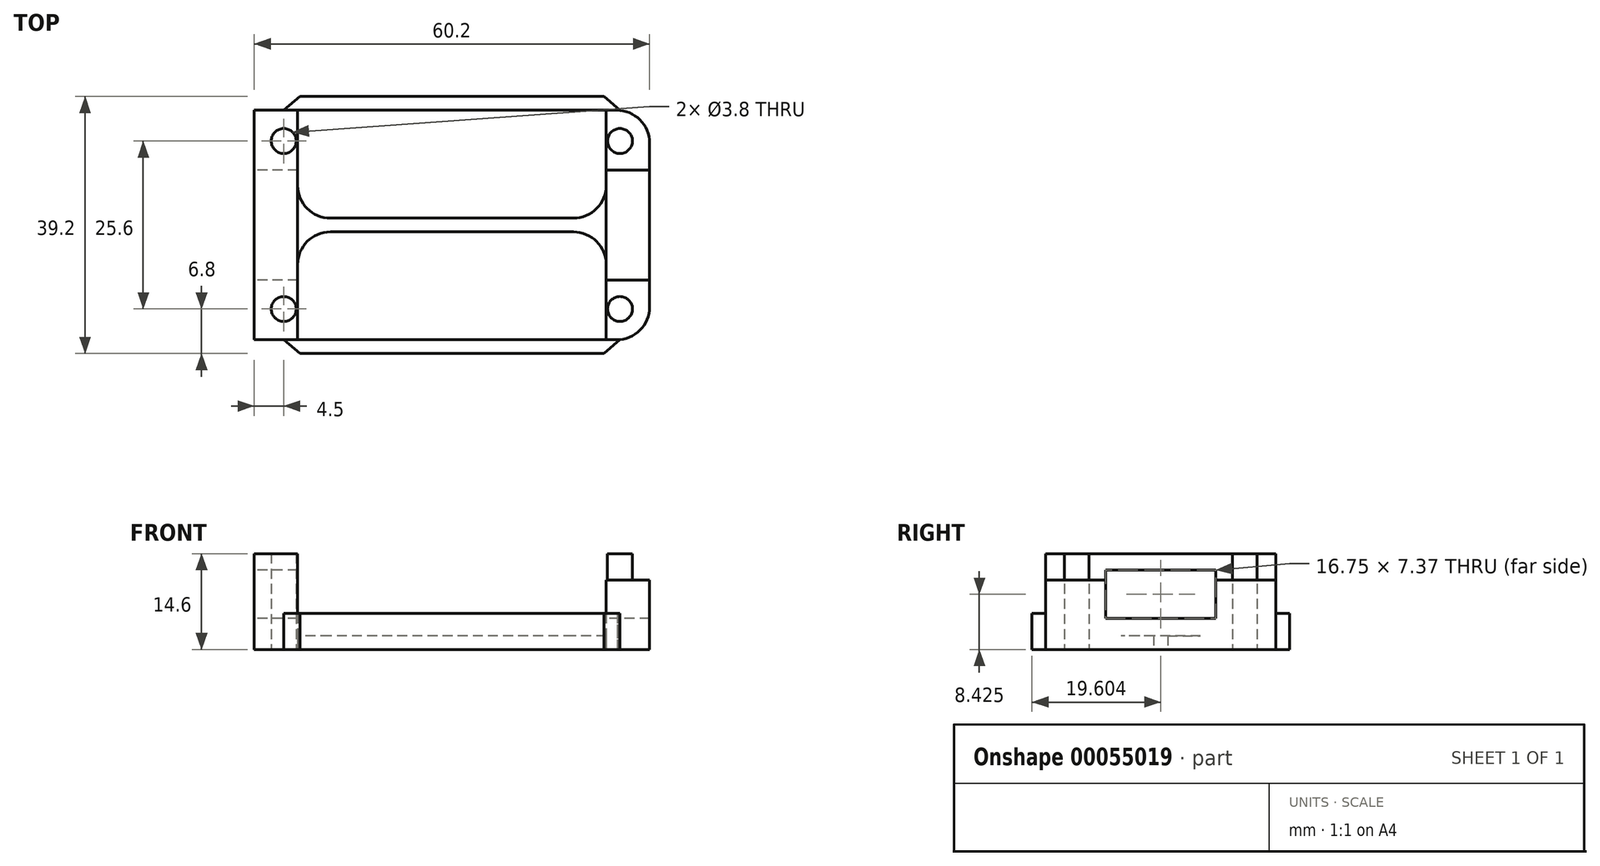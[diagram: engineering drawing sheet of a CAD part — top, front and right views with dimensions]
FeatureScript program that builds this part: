
annotation { "Feature Type Name" : "Feature", "Feature Type Description" : "" }
export const myFeature = defineFeature(function(context is Context, id is Id, definition is map)
    precondition{}
    {
        {
            var Q0;
            Q0=qCreatedBy(makeId("Top.planeOp"),FACE);
            var sketch = newSketch(context, id + "F0", { "sketchPlane" : qUnion([Q0])});
            skCircle(sketch, "E0", {"center": v(0, 0) * mm, "radius": 1.9 * mm});
            skCircle(sketch, "E1", {"center": v(0, -25.6) * mm, "radius": 1.9 * mm});
            skLineSegment(sketch, "E2.rect.bottom", {"start": v(2.1, -30.3) * mm, "end": v(-4.5, -30.3) * mm});
            skLineSegment(sketch, "E2.rect.right", {"start": v(-4.5, -30.3) * mm, "end": v(-4.5, 4.7) * mm});
            skPoint(sketch, "E2.rect.middle", {"position": v(0, -12.8) * mm});
            skLineSegment(sketch, "E3.MirrorCS", {"start": v(-4.58, -30.3) * mm, "end": v(-4.5, -30.3) * mm});
            skLineSegment(sketch, "E4.MirrorCS", {"start": v(-4.58, -30.3) * mm, "end": v(-4.58, 4.7) * mm});
            skLineSegment(sketch, "E5", {"start": v(2.1, -20.4) * mm, "end": v(2.1, -30.3) * mm});
            skLineSegment(sketch, "E6", {"start": v(2.1, -20.4) * mm, "end": v(2.1, -18.85) * mm});
            skLineSegment(sketch, "E7.trimOffspring", {"start": v(4.5, -30.3) * mm, "end": v(4.58, -30.3) * mm});
            skLineSegment(sketch, "E8", {"start": v(2.1, 4.7) * mm, "end": v(-4.5, 4.7) * mm});
            skPoint(sketch, "E9.MirrorP", {"position": v(51.2, -12.8) * mm});
            skCircle(sketch, "E10.MirrorC", {"center": v(51.2, -25.6) * mm, "radius": 1.9 * mm});
            skCircle(sketch, "E11.MirrorC", {"center": v(51.2, 0) * mm, "radius": 1.9 * mm});
            skLineSegment(sketch, "E12.MirrorCS", {"start": v(55.7, -30.3) * mm, "end": v(55.7, 4.7) * mm});
            skLineSegment(sketch, "E13.MirrorCS", {"start": v(49.1, -30.3) * mm, "end": v(55.7, -30.3) * mm});
            skLineSegment(sketch, "E14.MirrorCS", {"start": v(49.1, 4.7) * mm, "end": v(55.7, 4.7) * mm});
            skLineSegment(sketch, "E15.MirrorCS", {"start": v(49.1, -20.4) * mm, "end": v(49.1, -30.3) * mm});
            skLineSegment(sketch, "E16.MirrorCS", {"start": v(55.78, -30.3) * mm, "end": v(55.78, 4.7) * mm});
            skLineSegment(sketch, "E17.MirrorCS", {"start": v(49.1, -20.4) * mm, "end": v(49.1, -18.85) * mm});
            skLineSegment(sketch, "E18", {"start": v(55.78, -12.8) * mm, "end": v(55.7, -12.8) * mm});
            skLineSegment(sketch, "E19", {"start": v(25.64, -13.85) * mm, "end": v(44.1, -13.85) * mm});
            skLineSegment(sketch, "E20", {"start": v(25.64, -11.75) * mm, "end": v(44.1, -11.75) * mm});
            skLineSegment(sketch, "E21", {"start": v(25.64, -13.85) * mm, "end": v(7.1, -13.85) * mm});
            skLineSegment(sketch, "E22", {"start": v(25.64, -11.75) * mm, "end": v(7.1, -11.75) * mm});
            skLineSegment(sketch, "E23.trimOffspring", {"start": v(2.1, -6.75) * mm, "end": v(2.1, 4.7) * mm});
            skPoint(sketch, "E24.visualSharp", {"position": v(2.1, -11.75) * mm});
            skArc(sketch, "E24.filletArc", {"start": v(2.1, -6.75) * mm, "mid": v(3.56, -10.29) * mm, "end": v(7.1, -11.75) * mm});
            skPoint(sketch, "E25.visualSharp", {"position": v(2.1, -13.85) * mm});
            skArc(sketch, "E25.filletArc", {"start": v(7.1, -13.85) * mm, "mid": v(3.56, -15.31) * mm, "end": v(2.1, -18.85) * mm});
            skLineSegment(sketch, "E26.trimOffspring", {"start": v(49.1, -6.75) * mm, "end": v(49.1, 4.7) * mm});
            skArc(sketch, "E27.MirrorCS", {"start": v(49.1, -6.75) * mm, "mid": v(47.64, -10.29) * mm, "end": v(44.1, -11.75) * mm});
            skPoint(sketch, "E28.MirrorP", {"position": v(49.1, -13.85) * mm});
            skArc(sketch, "E29.MirrorCS", {"start": v(44.1, -13.85) * mm, "mid": v(47.64, -15.31) * mm, "end": v(49.1, -18.85) * mm});
            skPoint(sketch, "E30.MirrorP", {"position": v(49.1, -11.75) * mm});
            skPoint(sketch, "E31.start.orphan", {"position": v(25.64, -12.8) * mm});
            skPoint(sketch, "E32.trimOffspring.end.orphan", {"position": v(-4.5, -12.8) * mm});
            skPoint(sketch, "E33.start.orphan", {"position": v(25.6, -25.6) * mm});
            skPoint(sketch, "E34.start.orphan", {"position": v(25.6, -20.4) * mm});
            skLineSegment(sketch, "E35", {"start": v(2.1, -6.75) * mm, "end": v(2.1, -18.85) * mm});
            skLineSegment(sketch, "E36", {"start": v(49.1, -6.75) * mm, "end": v(49.1, -18.85) * mm});
            skSolve(sketch);
        }
        {
            var Q0;
            Q0=makeQuery(id+"F0.imprint","IMPRINT",FACE,{"disambiguationData":[TD([[makeQuery(id+"F0.imprint","IMPRINT",EDGE,{"derivedFrom":sQuery(id+"F0.wireOp",EDGE,"E1")}),-1.0]])]});
            var Q1;
            Q1=makeQuery(id+"F0.imprint","IMPRINT",FACE,{"disambiguationData":[TD([[makeQuery(id+"F0.imprint","IMPRINT",EDGE,{"derivedFrom":sQuery(id+"F0.wireOp",EDGE,"E0")}),-1.0]])]});
            var Q2;
            Q2=makeQuery(id+"F0.imprint","IMPRINT",FACE,{"disambiguationData":[TD([[makeQuery(id+"F0.imprint","IMPRINT",EDGE,{"derivedFrom":sQuery(id+"F0.wireOp",EDGE,"E11.MirrorC")}),1.0]])]});
            var Q3;
            Q3=makeQuery(id+"F0.imprint","IMPRINT",FACE,{"disambiguationData":[TD([[makeQuery(id+"F0.imprint","IMPRINT",EDGE,{"derivedFrom":sQuery(id+"F0.wireOp",EDGE,"E10.MirrorC")}),1.0]])]});
            extrude(context, id + "F1", {"entities" : qUnion([Q0, Q1, Q2, Q3]), "depth" : (8.5 + 2.1 + 4) * mm});
        }
        {
            var Q0;
            Q0=makeQuery(id+"F0.imprint","IMPRINT",FACE,{"disambiguationData":[TD([[makeQuery(id+"F0.imprint","IMPRINT",EDGE,{"derivedFrom":sQuery(id+"F0.wireOp",EDGE,"E2.rect.bottom")}),-1.0]])]});
            var Q1;
            Q1=makeQuery(id+"F0.imprint","IMPRINT",FACE,{"disambiguationData":[TD([[makeQuery(id+"F0.imprint","IMPRINT",EDGE,{"derivedFrom":sQuery(id+"F0.wireOp",EDGE,"E19")}),1.0]])]});
            var Q2;
            {var subQ1=sQuery(id+"F0.wireOp",EDGE,"E13.MirrorCS");Q2=makeQuery(id+"F0.imprint","IMPRINT",FACE,{"disambiguationData":[TD([[makeQuery(id+"F0.imprint","IMPRINT",EDGE,{"derivedFrom":subQ1}),1.0]])]});}
            extrude(context, id + "F2", {"entities" : qUnion([Q0, Q1, Q2]), "operationType" : NewBodyOperationType.ADD, "depth" : 2.1 * mm});
        }
        {
            var Q0;
            Q0=makeQuery(id+"F0.imprint","IMPRINT",FACE,{"disambiguationData":[TD([[makeQuery(id+"F0.imprint","IMPRINT",EDGE,{"derivedFrom":sQuery(id+"F0.wireOp",EDGE,"E2.rect.bottom")}),-1.0]])]});
            var Q1;
            {var subQ1=sQuery(id+"F0.wireOp",EDGE,"E13.MirrorCS");Q1=makeQuery(id+"F0.imprint","IMPRINT",FACE,{"disambiguationData":[TD([[makeQuery(id+"F0.imprint","IMPRINT",EDGE,{"derivedFrom":subQ1}),1.0]])]});}
            extrude(context, id + "F3", {"entities" : qUnion([Q0, Q1]), "operationType" : NewBodyOperationType.ADD, "depth" : (8.5 + 2.1) * mm});
        }
        {
            var Q0;
            Q0=qCreatedBy(makeId("Right.planeOp"),FACE);
            var sketch = newSketch(context, id + "F4", { "sketchPlane" : qUnion([Q0])});
            skLineSegment(sketch, "E37", {"start": v(-4.42, 12.11) * mm, "end": v(-21.17, 12.11) * mm});
            skLineSegment(sketch, "E38.rect.top", {"start": v(-21.17, 4.74) * mm, "end": v(-4.42, 4.74) * mm});
            skLineSegment(sketch, "E38.rect.left", {"start": v(-21.17, 12.11) * mm, "end": v(-21.17, 4.74) * mm});
            skLineSegment(sketch, "E38.rect.right", {"start": v(-4.42, 12.11) * mm, "end": v(-4.42, 4.74) * mm});
            skPoint(sketch, "E38.rect.middle", {"position": v(-12.8, 12.11) * mm});
            skPoint(sketch, "E39.orphan", {"position": v(4.7, 12.11) * mm});
            skPoint(sketch, "E38.rect.bottom.end.orphan", {"position": v(-4.42, 19.49) * mm});
            skPoint(sketch, "E40.orphan", {"position": v(-21.17, 19.49) * mm});
            skPoint(sketch, "E41.orphan", {"position": v(-30.3, 12.11) * mm});
            skSolve(sketch);
        }
        {
            var Q0;
            Q0=makeQuery(id+"F4.imprint","IMPRINT",FACE,{"disambiguationData":[TD([[makeQuery(id+"F4.imprint","IMPRINT",EDGE,{"derivedFrom":sQuery(id+"F4.wireOp",EDGE,"E37")}),1.0]])]});
            extrude(context, id + "F5", {"entities" : qUnion([Q0]), "operationType" : NewBodyOperationType.REMOVE, "endBound" : BoundingType.SYMMETRIC, "depth" : 300 * mm});
        }
        {
            var Q0;
            {var subQ0=sQuery(id+"F0.wireOp",EDGE,"E14.MirrorCS");var subQ1=sQuery(id+"F0.wireOp",EDGE,"E12.MirrorCS");Q0=makeQuery(id+"F3.boolean.opBoolean","MERGE",EDGE,{"derivedFrom":[makeQuery(id+"F2.opExtrude","SWEPT_EDGE",EDGE,{"disambiguationData":[OSD([subQ1,subQ0])]}),makeQuery(id+"F3.opExtrude","SWEPT_EDGE",EDGE,{"disambiguationData":[OSD([subQ1,subQ0])]})]});}
            var Q1;
            {var subQ0=sQuery(id+"F0.wireOp",EDGE,"E13.MirrorCS");var subQ1=sQuery(id+"F0.wireOp",EDGE,"E12.MirrorCS");Q1=makeQuery(id+"F3.boolean.opBoolean","MERGE",EDGE,{"derivedFrom":[makeQuery(id+"F2.opExtrude","SWEPT_EDGE",EDGE,{"disambiguationData":[OSD([subQ1,subQ0])]}),makeQuery(id+"F3.opExtrude","SWEPT_EDGE",EDGE,{"disambiguationData":[OSD([subQ1,subQ0])]})]});}
            var Q2;
            {var subQ0=sQuery(id+"F0.wireOp",EDGE,"E8");var subQ1=sQuery(id+"F0.wireOp",EDGE,"E2.rect.right");Q2=makeQuery(id+"F3.boolean.opBoolean","MERGE",EDGE,{"derivedFrom":[makeQuery(id+"F2.opExtrude","SWEPT_EDGE",EDGE,{"disambiguationData":[OSD([subQ1,subQ0])]}),makeQuery(id+"F3.opExtrude","SWEPT_EDGE",EDGE,{"disambiguationData":[OSD([subQ1,subQ0])]})]});}
            var Q3;
            {var subQ0=sQuery(id+"F0.wireOp",EDGE,"E2.rect.right");var subQ1=sQuery(id+"F0.wireOp",EDGE,"E2.rect.bottom");Q3=makeQuery(id+"F3.boolean.opBoolean","MERGE",EDGE,{"derivedFrom":[makeQuery(id+"F2.opExtrude","SWEPT_EDGE",EDGE,{"disambiguationData":[OSD([subQ1,subQ0])]}),makeQuery(id+"F3.opExtrude","SWEPT_EDGE",EDGE,{"disambiguationData":[OSD([subQ1,subQ0])]})]});}
            fillet(context, id + "F6", {"entities" : qUnion([Q0, Q1, Q2, Q3]), "radius" : 5 * mm, "tangentPropagation" : true, "allowEdgeOverflow" : false});
        }
        {
            var Q0;
            Q0=qCreatedBy(makeId("Top.planeOp"),FACE);
            var sketch = newSketch(context, id + "F7", { "sketchPlane" : qUnion([Q0])});
            skLineSegment(sketch, "E42", {"start": v(9.95, -12.8) * mm, "end": v(56.97, -12.8) * mm});
            skLineSegment(sketch, "E43.MirrorCS", {"start": v(9.95, -30.3) * mm, "end": v(7.5, -30.3) * mm});
            skLineSegment(sketch, "E44.MirrorCS", {"start": v(9.95, -32.4) * mm, "end": v(25.6, -32.4) * mm});
            skLineSegment(sketch, "E45.MirrorCS", {"start": v(9.95, -30.3) * mm, "end": v(25.6, -30.3) * mm});
            skLineSegment(sketch, "E46.MirrorCS", {"start": v(25.6, -30.3) * mm, "end": v(9.95, -30.3) * mm});
            skLineSegment(sketch, "E47.MirrorCS", {"start": v(25.6, -32.4) * mm, "end": v(9.95, -32.4) * mm});
            skLineSegment(sketch, "E48", {"start": v(7.5, -30.3) * mm, "end": v(0, -30.3) * mm});
            skLineSegment(sketch, "E49", {"start": v(0, -30.3) * mm, "end": v(2.44, -32.4) * mm});
            skLineSegment(sketch, "E50", {"start": v(2.44, -32.4) * mm, "end": v(9.95, -32.4) * mm});
            skPoint(sketch, "E51.orphan", {"position": v(9.95, -30.3) * mm});
            skLineSegment(sketch, "E52", {"start": v(0, -25.72) * mm, "end": v(51.2, -25.72) * mm});
            skLineSegment(sketch, "E53", {"start": v(25.6, -25.72) * mm, "end": v(25.6, -30.3) * mm});
            skLineSegment(sketch, "E54.trimOffspring", {"start": v(25.6, -32.4) * mm, "end": v(25.6, -35.26) * mm});
            skLineSegment(sketch, "E55.MirrorCS", {"start": v(41.25, -32.4) * mm, "end": v(25.6, -32.4) * mm});
            skLineSegment(sketch, "E56.MirrorCS", {"start": v(41.25, -30.3) * mm, "end": v(25.6, -30.3) * mm});
            skLineSegment(sketch, "E57.MirrorCS", {"start": v(25.6, -32.4) * mm, "end": v(41.25, -32.4) * mm});
            skLineSegment(sketch, "E58.MirrorCS", {"start": v(25.6, -30.3) * mm, "end": v(41.25, -30.3) * mm});
            skLineSegment(sketch, "E59.MirrorCS", {"start": v(41.25, -30.3) * mm, "end": v(43.7, -30.3) * mm});
            skLineSegment(sketch, "E60.MirrorCS", {"start": v(51.2, -30.3) * mm, "end": v(48.75, -32.4) * mm});
            skLineSegment(sketch, "E61.MirrorCS", {"start": v(43.7, -30.3) * mm, "end": v(51.2, -30.3) * mm});
            skLineSegment(sketch, "E62.MirrorCS", {"start": v(48.75, -32.4) * mm, "end": v(41.25, -32.4) * mm});
            skPoint(sketch, "E63.MirrorP", {"position": v(41.25, -30.3) * mm});
            skLineSegment(sketch, "E64.MirrorCS", {"start": v(25.6, 4.7) * mm, "end": v(41.25, 4.7) * mm});
            skLineSegment(sketch, "E65.MirrorCS", {"start": v(9.95, 6.8) * mm, "end": v(25.6, 6.8) * mm});
            skLineSegment(sketch, "E66.MirrorCS", {"start": v(41.25, 6.8) * mm, "end": v(25.6, 6.8) * mm});
            skLineSegment(sketch, "E67.MirrorCS", {"start": v(9.95, 4.7) * mm, "end": v(7.5, 4.7) * mm});
            skLineSegment(sketch, "E68.MirrorCS", {"start": v(41.25, 4.7) * mm, "end": v(43.7, 4.7) * mm});
            skLineSegment(sketch, "E69.MirrorCS", {"start": v(9.95, 4.7) * mm, "end": v(25.6, 4.7) * mm});
            skLineSegment(sketch, "E70.MirrorCS", {"start": v(43.7, 4.7) * mm, "end": v(51.2, 4.7) * mm});
            skLineSegment(sketch, "E71.MirrorCS", {"start": v(0, 4.7) * mm, "end": v(2.44, 6.8) * mm});
            skPoint(sketch, "E72.MirrorP", {"position": v(41.25, 4.7) * mm});
            skLineSegment(sketch, "E73.MirrorCS", {"start": v(51.2, 4.7) * mm, "end": v(48.75, 6.8) * mm});
            skLineSegment(sketch, "E74.MirrorCS", {"start": v(2.44, 6.8) * mm, "end": v(9.95, 6.8) * mm});
            skLineSegment(sketch, "E75.MirrorCS", {"start": v(7.5, 4.7) * mm, "end": v(0, 4.7) * mm});
            skLineSegment(sketch, "E76.MirrorCS", {"start": v(41.25, 4.7) * mm, "end": v(25.6, 4.7) * mm});
            skLineSegment(sketch, "E77.MirrorCS", {"start": v(25.6, 6.8) * mm, "end": v(41.25, 6.8) * mm});
            skPoint(sketch, "E78.MirrorP", {"position": v(9.95, 4.7) * mm});
            skLineSegment(sketch, "E79.MirrorCS", {"start": v(25.6, 4.7) * mm, "end": v(9.95, 4.7) * mm});
            skLineSegment(sketch, "E80.MirrorCS", {"start": v(48.75, 6.8) * mm, "end": v(41.25, 6.8) * mm});
            skLineSegment(sketch, "E81.MirrorCS", {"start": v(25.6, 6.8) * mm, "end": v(9.95, 6.8) * mm});
            skSolve(sketch);
        }
        {
            var Q0;
            Q0=makeQuery(id+"F7.imprint","IMPRINT",FACE,{"disambiguationData":[TD([[makeQuery(id+"F7.imprint","IMPRINT",EDGE,{"derivedFrom":sQuery(id+"F7.wireOp",EDGE,"E43.MirrorCS")}),1.0]])]});
            var Q1;
            Q1=makeQuery(id+"F7.imprint","IMPRINT",FACE,{"disambiguationData":[TD([[makeQuery(id+"F7.imprint","IMPRINT",EDGE,{"derivedFrom":sQuery(id+"F7.wireOp",EDGE,"E70.MirrorCS")}),1.0]])]});
            extrude(context, id + "F8", {"entities" : qUnion([Q0, Q1]), "operationType" : NewBodyOperationType.ADD, "depth" : 5.5 * mm});
        }
    });
